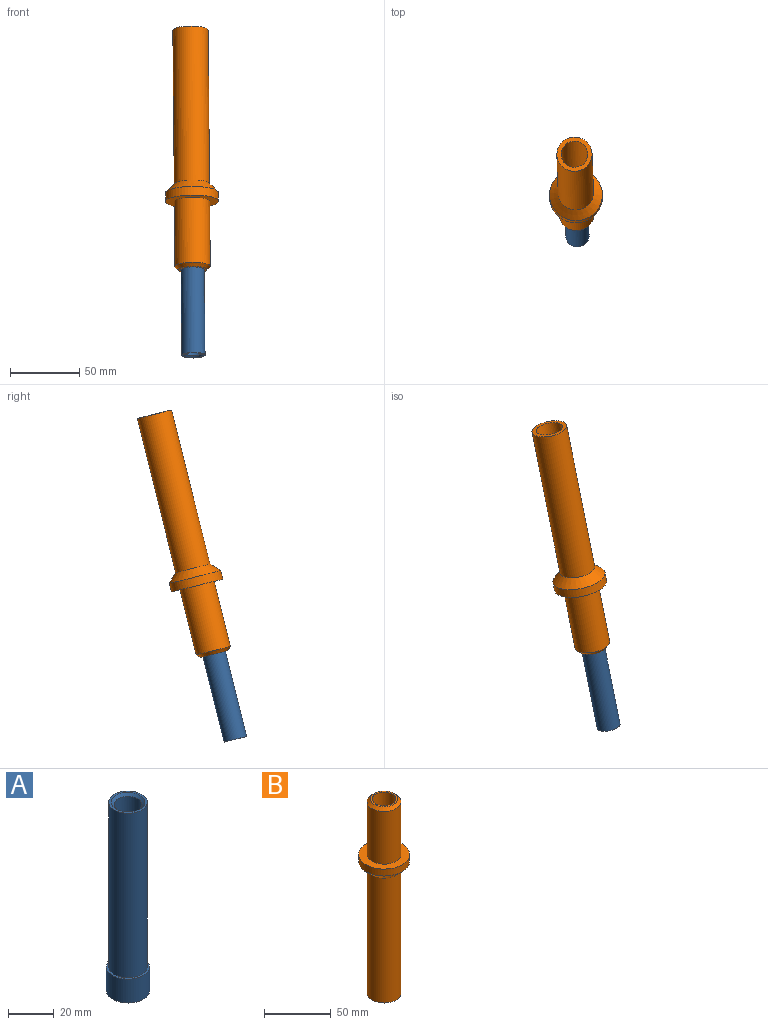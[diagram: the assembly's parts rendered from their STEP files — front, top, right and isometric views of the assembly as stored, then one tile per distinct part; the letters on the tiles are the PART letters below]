
ASSEMBLY  parts=2 mates=1
PART A: 9 faces, bbox 18.8x18.8x100.3 mm
  f0: plane 12.19x12.19mm, normal (0,0,1), area 85.1mm2, adj f4,f7
  f1: cylinder r=9.4mm len=18.8mm, axis (0,0,1), area 749.9mm2, adj f2,f3
  f2: plane 18.8x18.8mm, normal (0,0,-1), area 245.8mm2, adj f1,f4
  f3: plane 18.8x18.8mm, normal (0,0,1), area 56.8mm2, adj f1,f5
  f4: cylinder r=3.17mm len=12.7mm, axis (0,0,1), area 253.4mm2, adj f0,f2
  f5: cylinder r=8.38mm len=87.63mm, axis (0,0,-1), area 4615.1mm2, adj f3,f6
  f6: plane 16.76x16.76mm, normal (0,0,1), area 50.3mm2, adj f5,f8
  f7: cylinder r=6.1mm len=86.36mm, axis (0,0,-1), area 3307.8mm2, adj f0,f8
  f8: cone r=7.37mm half-angle=45deg, axis (0,0,1), area 76mm2, adj f6,f7
PART B: 11 faces, bbox 38.1x38.1x177.8 mm
  f0: plane 19.3x19.3mm, normal (0,0,-1), area 51.4mm2, adj f3,f9
  f1: cylinder r=12.7mm len=48.26mm, axis (0,0,-1), area 3851mm2, adj f4,f6
  f2: plane 20.32x20.32mm, normal (0,0,1), area 83mm2, adj f3,f4
  f3: cylinder r=8.76mm len=63.5mm, axis (0,0,-1), area 3496.3mm2, adj f0,f2
  f4: cone r=10.16mm half-angle=45deg, axis (0,0,-1), area 258mm2, adj f1,f2
  f5: cylinder r=19.05mm len=38.1mm, axis (0,0,-1), area 760.1mm2, adj f6,f10
  f6: plane 38.1x38.1mm, normal (0,0,1), area 633.4mm2, adj f1,f5
  f7: cylinder r=12.7mm len=114.3mm, axis (0,0,1), area 9120.7mm2, adj f8,f10
  f8: plane 25.4x25.4mm, normal (0,0,-1), area 214mm2, adj f7,f9
  f9: cylinder r=9.65mm len=114.3mm, axis (0,0,1), area 6931.8mm2, adj f0,f8
  f10: cone r=19.05mm half-angle=45deg, axis (0,0,1), area 895.7mm2, adj f5,f7
PLACE A rot(axis=(1,0.1,-0.01),166deg) t=(66.39,36.43,-105.99)mm
PLACE B rot(axis=(0.73,-0.67,0.09),170.1deg) t=(66.05,45.89,-67.98)mm
MATE cylindrical B.f1 <-> A.f1  axis (0.01,-0.24,-0.97) through (65.55,59.68,-12.52)mm
